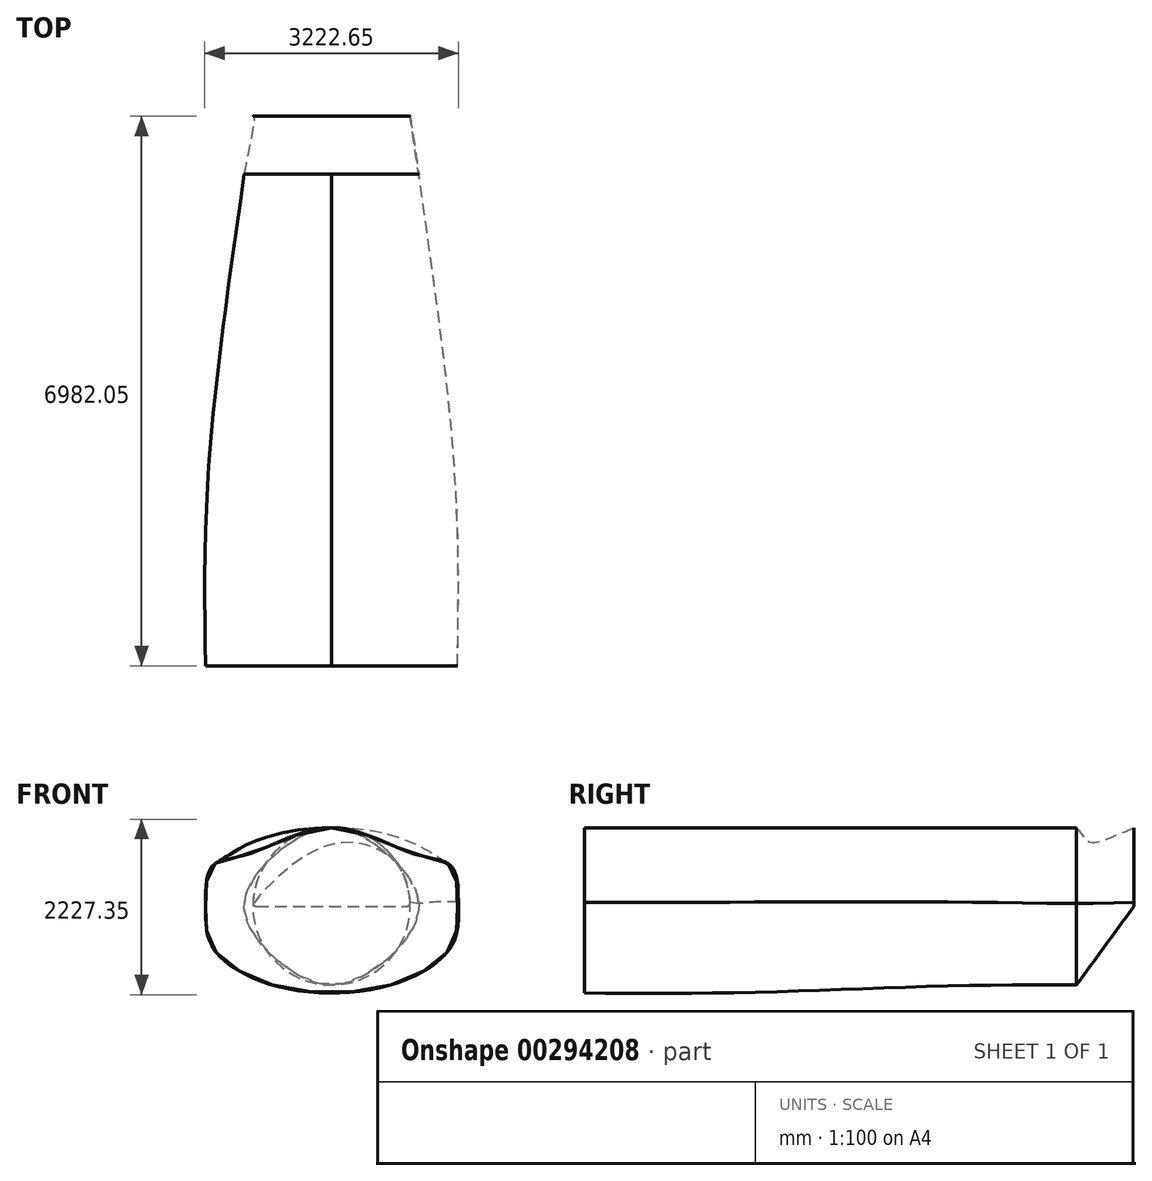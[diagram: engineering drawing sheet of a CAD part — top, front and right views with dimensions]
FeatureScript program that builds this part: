
annotation { "Feature Type Name" : "Feature", "Feature Type Description" : "" }
export const myFeature = defineFeature(function(context is Context, id is Id, definition is map)
    precondition{}
    {
        {
            var Q0;
            Q0=qCreatedBy(makeId("Front.planeOp"),FACE);
            cPlane(context, id + "F0", {"entities" : qUnion([Q0]), "cplaneType" : CPlaneType.OFFSET, "offset" : 1750 * mm, "width" : 150 * mm, "height" : 150 * mm});
        }
        {
            var Q0;
            Q0=qCreatedBy(id+"F0.planeOp",FACE);
            var sketch = newSketch(context, id + "F1", { "sketchPlane" : qUnion([Q0])});
            skPoint(sketch, "E0.middle", {"position": v(0, 0) * mm});
            skFitSpline(sketch, "E1", {"points": [v(0, 1000) * mm, v(1060, 662.5) * mm, v(1517.6, 506.84) * mm, v(1600, 0) * mm, v(1517.6, -506.84) * mm, v(750, -1000) * mm, v(-750, -1000) * mm, v(-1517.6, -506.84) * mm, v(-1600, 0) * mm, v(-1517.6, 506.84) * mm, v(-1060, 662.5) * mm, v(0, 1000) * mm]});
            skSolve(sketch);
        }
        {
            var Q0;
            Q0=qCreatedBy(makeId("Front.planeOp"),FACE);
            var sketch = newSketch(context, id + "F2", { "sketchPlane" : qUnion([Q0])});
            skPoint(sketch, "E2.middle", {"position": v(0, 0) * mm});
            skFitSpline(sketch, "E3", {"points": [v(0, 1000) * mm, v(1060, 662.5) * mm, v(1517.6, 506.84) * mm, v(1600, 0) * mm, v(1517.6, -506.84) * mm, v(750, -1000) * mm, v(-750, -1000) * mm, v(-1517.6, -506.84) * mm, v(-1600, 0) * mm, v(-1517.6, 506.84) * mm, v(-1060, 662.5) * mm, v(0, 1000) * mm]});
            skSolve(sketch);
        }
        {
            var Q0;
            Q0=qCreatedBy(makeId("Front.planeOp"),FACE);
            cPlane(context, id + "F3", {"entities" : qUnion([Q0]), "cplaneType" : CPlaneType.OFFSET, "offset" : 3500 * mm, "oppositeDirection" : true, "width" : 150 * mm, "height" : 150 * mm});
        }
        {
            var Q0;
            Q0=qCreatedBy(id+"F3.planeOp",FACE);
            var sketch = newSketch(context, id + "F4", { "sketchPlane" : qUnion([Q0])});
            skPoint(sketch, "E4.middle", {"position": v(0, 0) * mm});
            skFitSpline(sketch, "E5", {"points": [v(0, 1000) * mm, v(1060, 662.5) * mm, v(1250, 0) * mm, v(1060, -662.5) * mm, v(0, -1000) * mm, v(-1060, -662.5) * mm, v(-1250, 0) * mm, v(-1060, 662.5) * mm, v(0, 1000) * mm]});
            skSolve(sketch);
        }
        {
            var Q0;
            Q0=qCreatedBy(makeId("Front.planeOp"),FACE);
            cPlane(context, id + "F5", {"entities" : qUnion([Q0]), "cplaneType" : CPlaneType.OFFSET, "offset" : 4500 * mm, "oppositeDirection" : true, "width" : 150 * mm, "height" : 150 * mm});
        }
        {
            var Q0;
            Q0=qCreatedBy(id+"F5.planeOp",FACE);
            var sketch = newSketch(context, id + "F6", { "sketchPlane" : qUnion([Q0])});
            skPoint(sketch, "E6.middle", {"position": v(0, 0) * mm});
            skFitSpline(sketch, "E7", {"points": [v(0, 1000) * mm, v(848, 530) * mm, v(1108.5, 0) * mm, v(848, -530) * mm, v(0, -1000) * mm, v(-848, -530) * mm, v(-1108.5, 0) * mm, v(-848, 530) * mm, v(0, 1000) * mm]});
            skSolve(sketch);
        }
        {
            var Q0;
            Q0=makeQuery(id+"F1.imprint","IMPRINT",FACE,{"disambiguationData":[TD([[makeQuery(id+"F1.imprint","IMPRINT",EDGE,{"derivedFrom":sQuery(id+"F1.wireOp",EDGE,"E1")}),-1.0]])]});
            var Q1;
            Q1=makeQuery(id+"F2.imprint","IMPRINT",FACE,{"disambiguationData":[TD([[makeQuery(id+"F2.imprint","IMPRINT",EDGE,{"derivedFrom":sQuery(id+"F2.wireOp",EDGE,"E3")}),-1.0]])]});
            var Q2;
            Q2=makeQuery(id+"F4.imprint","IMPRINT",FACE,{"disambiguationData":[TD([[makeQuery(id+"F4.imprint","IMPRINT",EDGE,{"derivedFrom":sQuery(id+"F4.wireOp",EDGE,"E5")}),-1.0]])]});
            var Q3;
            Q3=makeQuery(id+"F6.imprint","IMPRINT",FACE,{"disambiguationData":[TD([[makeQuery(id+"F6.imprint","IMPRINT",EDGE,{"derivedFrom":sQuery(id+"F6.wireOp",EDGE,"E7")}),-1.0]])]});
            loft(context, id + "F7", {"sheetProfilesArray" : [{ "sheetProfileEntities" : qUnion([Q0]) }, { "sheetProfileEntities" : qUnion([Q1]) }, { "sheetProfileEntities" : qUnion([Q2]) }, { "sheetProfileEntities" : qUnion([Q3]) }]});
        }
        {
            var Q0;
            Q0=qCreatedBy(makeId("Front.planeOp"),FACE);
            cPlane(context, id + "F8", {"entities" : qUnion([Q0]), "cplaneType" : CPlaneType.OFFSET, "offset" : 5232.05 * mm, "oppositeDirection" : true, "width" : 150 * mm, "height" : 150 * mm});
        }
        {
            var Q0;
            Q0=qCreatedBy(id+"F8.planeOp",FACE);
            var sketch = newSketch(context, id + "F9", { "sketchPlane" : qUnion([Q0])});
            skArc(sketch, "E8", {"start": v(998.61, 52.63) * mm, "mid": v(0, 1000) * mm, "end": v(-998.61, 52.63) * mm});
            skLineSegment(sketch, "E9", {"start": v(-948.68, 0) * mm, "end": v(948.68, 0) * mm});
            skArc(sketch, "E10.filletArc", {"start": v(-998.61, 52.63) * mm, "mid": v(-984.96, 15.59) * mm, "end": v(-948.68, 0) * mm});
            skArc(sketch, "E11.filletArc", {"start": v(948.68, 0) * mm, "mid": v(984.96, 15.59) * mm, "end": v(998.61, 52.63) * mm});
            skPoint(sketch, "E12", {"position": v(0, 1000) * mm});
            skPoint(sketch, "E13", {"position": v(-948.68, 316.23) * mm});
            skPoint(sketch, "E14", {"position": v(948.68, 316.23) * mm});
            skPoint(sketch, "E15", {"position": v(-661.44, 750) * mm});
            skPoint(sketch, "E16", {"position": v(661.44, 750) * mm});
            skPoint(sketch, "E17", {"position": v(-661.44, 0) * mm});
            skPoint(sketch, "E18", {"position": v(661.44, 0) * mm});
            skPoint(sketch, "E19", {"position": v(0, 500) * mm});
            skSolve(sketch);
        }
        {
            var Q0;
            Q0 = qSketchRegion(id + "F1", true);
            var Q1;
            Q1 = qSketchRegion(id + "F2", true);
            var Q2;
            Q2 = qSketchRegion(id + "F4", true);
            var Q3;
            Q3 = qSketchRegion(id + "F6", true);
            var Q4;
            Q4 = qSketchRegion(id + "F9", true);
            loft(context, id + "F10", {"sheetProfilesArray" : [{ "sheetProfileEntities" : qUnion([Q0]) }, { "sheetProfileEntities" : qUnion([Q1]) }, { "sheetProfileEntities" : qUnion([Q2]) }, { "sheetProfileEntities" : qUnion([Q3]) }, { "sheetProfileEntities" : qUnion([Q4]) }]});
        }
        {
            var Q0;
            Q0 = qSketchRegion(id + "F6", true);
            var Q1;
            Q1 = qSketchRegion(id + "F9", true);
            loft(context, id + "F11", {"sheetProfilesArray" : [{ "sheetProfileEntities" : qUnion([Q0]) }, { "sheetProfileEntities" : qUnion([Q1]) }]});
        }
        {
            var Q0;
            Q0 = qSketchRegion(id + "F6", true);
            var Q1;
            Q1 = qSketchRegion(id + "F9", true);
            loft(context, id + "F12", {"sheetProfilesArray" : [{ "sheetProfileEntities" : qUnion([Q0]) }, { "sheetProfileEntities" : qUnion([Q1]) }]});
        }
        {
            var Q0;
            Q0 = qSketchRegion(id + "F1", true);
            var Q1;
            Q1 = qSketchRegion(id + "F2", true);
            var Q2;
            Q2 = qSketchRegion(id + "F4", true);
            var Q3;
            Q3 = qSketchRegion(id + "F6", true);
            var Q4;
            Q4 = qSketchRegion(id + "F9", true);
            loft(context, id + "F13", {"sheetProfilesArray" : [{ "sheetProfileEntities" : qUnion([Q0]) }, { "sheetProfileEntities" : qUnion([Q1]) }, { "sheetProfileEntities" : qUnion([Q2]) }, { "sheetProfileEntities" : qUnion([Q3]) }, { "sheetProfileEntities" : qUnion([Q4]) }]});
        }
        {
            var Q0;
            Q0 = qSketchRegion(id + "F1", true);
            var Q1;
            Q1 = qSketchRegion(id + "F2", true);
            var Q2;
            Q2 = qSketchRegion(id + "F4", true);
            var Q3;
            Q3 = qSketchRegion(id + "F6", true);
            var Q4;
            Q4 = qSketchRegion(id + "F9", true);
            loft(context, id + "F14", {"sheetProfilesArray" : [{ "sheetProfileEntities" : qUnion([Q0]) }, { "sheetProfileEntities" : qUnion([Q1]) }, { "sheetProfileEntities" : qUnion([Q2]) }, { "sheetProfileEntities" : qUnion([Q3]) }, { "sheetProfileEntities" : qUnion([Q4]) }]});
        }
        {
            var Q0;
            Q0 = qSketchRegion(id + "F6", true);
            var Q1;
            Q1 = qSketchRegion(id + "F9", true);
            loft(context, id + "F15", {"sheetProfilesArray" : [{ "sheetProfileEntities" : qUnion([Q0]) }, { "sheetProfileEntities" : qUnion([Q1]) }]});
        }
        {
            var Q0;
            Q0=qCreatedBy(makeId("Front.planeOp"),FACE);
            cPlane(context, id + "F16", {"entities" : qUnion([Q0]), "cplaneType" : CPlaneType.OFFSET, "offset" : 4866.03 * mm, "oppositeDirection" : true, "width" : 150 * mm, "height" : 150 * mm});
        }
        {
            var Q0;
            Q0 = qSketchRegion(id + "F6", true);
            var Q1;
            Q1 = qSketchRegion(id + "F9", true);
            loft(context, id + "F17", {"sheetProfilesArray" : [{ "sheetProfileEntities" : qUnion([Q0]) }, { "sheetProfileEntities" : qUnion([Q1]) }]});
        }
        {
            var Q0;
            Q0 = qSketchRegion(id + "F6", true);
            var Q1;
            Q1 = qSketchRegion(id + "F9", true);
            loft(context, id + "F18", {"sheetProfilesArray" : [{ "sheetProfileEntities" : qUnion([Q0]) }, { "sheetProfileEntities" : qUnion([Q1]) }]});
        }
    });
